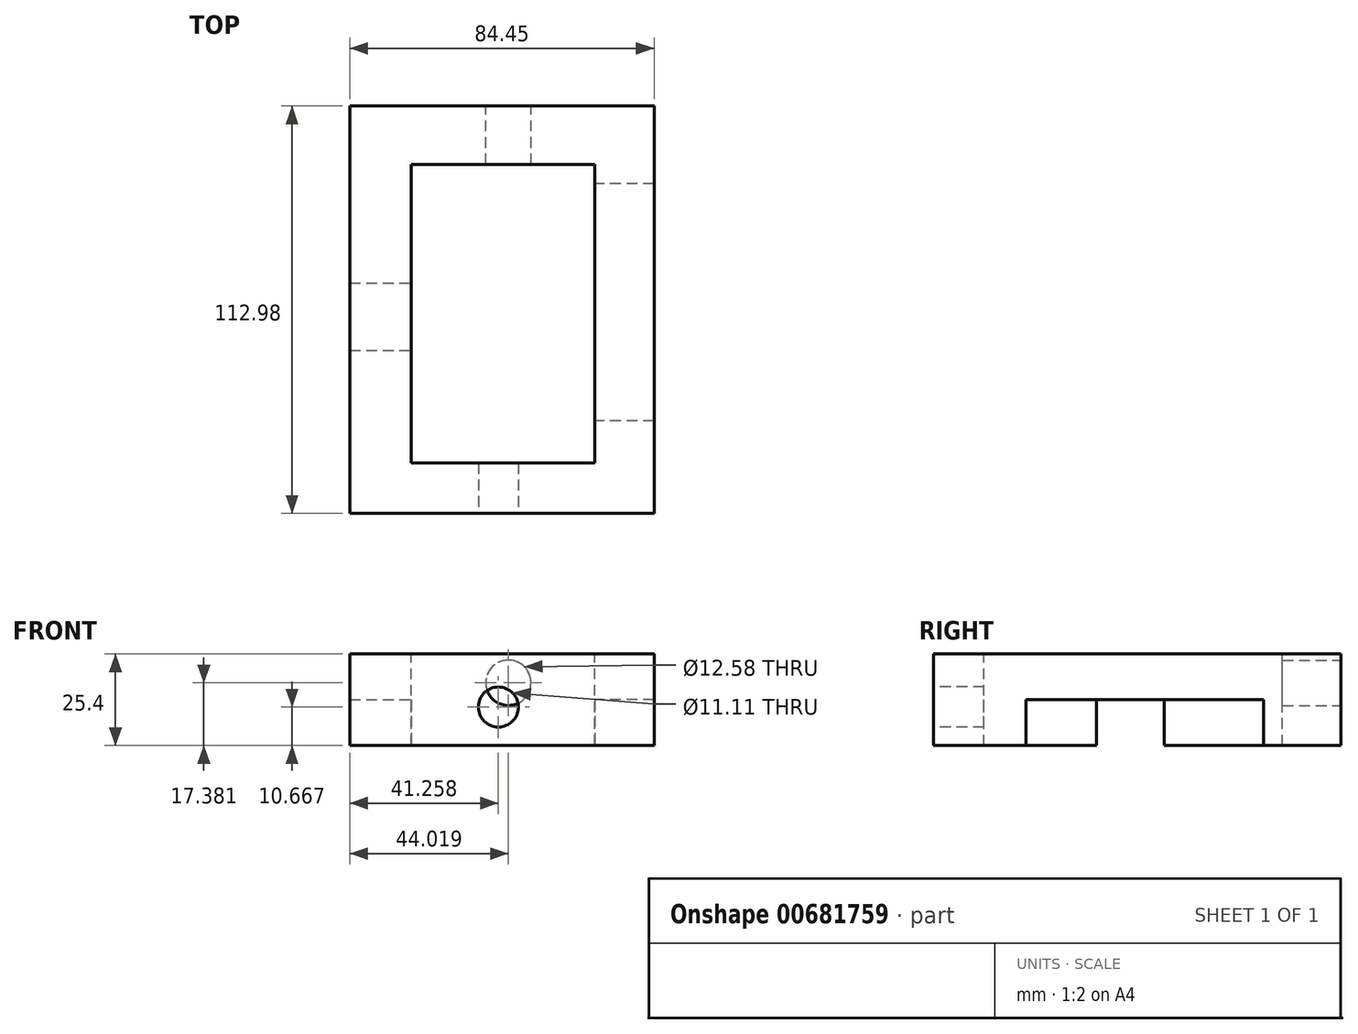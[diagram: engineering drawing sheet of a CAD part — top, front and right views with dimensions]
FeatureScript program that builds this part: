
annotation { "Feature Type Name" : "Feature", "Feature Type Description" : "" }
export const myFeature = defineFeature(function(context is Context, id is Id, definition is map)
    precondition{}
    {
        {
            var Q0;
            Q0=qCreatedBy(makeId("Top.planeOp"),FACE);
            var sketch = newSketch(context, id + "F0", { "sketchPlane" : qUnion([Q0])});
            skLineSegment(sketch, "E0.bottom", {"start": v(-38.24, 59.85) * mm, "end": v(46.21, 59.85) * mm});
            skLineSegment(sketch, "E0.top", {"start": v(-38.24, -53.13) * mm, "end": v(46.21, -53.13) * mm});
            skLineSegment(sketch, "E0.left", {"start": v(-38.24, 59.85) * mm, "end": v(-38.24, -53.13) * mm});
            skLineSegment(sketch, "E0.right", {"start": v(46.21, 59.85) * mm, "end": v(46.21, -53.13) * mm});
            skSolve(sketch);
        }
        {
            var Q0;
            Q0=makeQuery(id+"F0.imprint","IMPRINT",FACE,{"disambiguationData":[TD([[makeQuery(id+"F0.imprint","IMPRINT",EDGE,{"derivedFrom":sQuery(id+"F0.wireOp",EDGE,"E0.bottom")}),-1.0]])]});
            var Q1;
            Q1 = qSketchRegion(id + "F0", true);
            extrude(context, id + "F1", {"entities" : qUnion([Q0, Q1]), "depth" : 25.4 * mm, "offsetDistance" : 25.4 * mm});
        }
        {
            var Q0;
            Q0=makeQuery(id+"F1.opExtrude","CAP_FACE",FACE,{"disambiguationData":[OSD([sQuery(id+"F0.wireOp",EDGE,"E0.bottom"),sQuery(id+"F0.wireOp",EDGE,"E0.top"),sQuery(id+"F0.wireOp",EDGE,"E0.left"),sQuery(id+"F0.wireOp",EDGE,"E0.right")])],"isStart":false});
            var sketch = newSketch(context, id + "F2", { "sketchPlane" : qUnion([Q0])});
            skLineSegment(sketch, "E1.bottom", {"start": v(-21.11, 43.67) * mm, "end": v(29.77, 43.67) * mm});
            skLineSegment(sketch, "E1.top", {"start": v(-21.11, -39.16) * mm, "end": v(29.77, -39.16) * mm});
            skLineSegment(sketch, "E1.left", {"start": v(-21.11, 43.67) * mm, "end": v(-21.11, -39.16) * mm});
            skLineSegment(sketch, "E1.right", {"start": v(29.77, 43.67) * mm, "end": v(29.77, -39.16) * mm});
            skSolve(sketch);
        }
        {
            var Q0;
            Q0=makeQuery(id+"F2.imprint","IMPRINT",FACE,{"disambiguationData":[TD([[makeQuery(id+"F2.imprint","IMPRINT",EDGE,{"derivedFrom":sQuery(id+"F2.wireOp",EDGE,"E1.bottom")}),-1.0]])]});
            extrude(context, id + "F3", {"entities" : qUnion([Q0]), "operationType" : NewBodyOperationType.REMOVE, "oppositeDirection" : true, "depth" : 25.4 * mm, "offsetDistance" : 25.4 * mm});
        }
        {
            var Q0;
            Q0=makeQuery(id+"F1.opExtrude","SWEPT_FACE",FACE,{"disambiguationData":[OSD([sQuery(id+"F0.wireOp",EDGE,"E0.bottom")])]});
            var sketch = newSketch(context, id + "F4", { "sketchPlane" : qUnion([Q0])});
            skCircle(sketch, "E2", {"center": v(-5.78, 17.38) * mm, "radius": 6.29 * mm});
            skSolve(sketch);
        }
        {
            var Q0;
            Q0 = qSketchRegion(id + "F4", true);
            var Q1;
            Q1=makeQuery(id+"F4.imprint","IMPRINT",FACE,{"disambiguationData":[TD([[makeQuery(id+"F4.imprint","IMPRINT",EDGE,{"derivedFrom":sQuery(id+"F4.wireOp",EDGE,"E2")}),1.0]])]});
            extrude(context, id + "F5", {"entities" : qUnion([Q0, Q1]), "operationType" : NewBodyOperationType.REMOVE, "oppositeDirection" : true, "depth" : 25.4 * mm, "offsetDistance" : 25.4 * mm});
        }
        {
            var Q0;
            Q0=makeQuery(id+"F1.opExtrude","SWEPT_FACE",FACE,{"disambiguationData":[OSD([sQuery(id+"F0.wireOp",EDGE,"E0.top")])]});
            var sketch = newSketch(context, id + "F6", { "sketchPlane" : qUnion([Q0])});
            skCircle(sketch, "E3", {"center": v(3.02, 10.67) * mm, "radius": 5.56 * mm});
            skSolve(sketch);
        }
        {
            var Q0;
            Q0 = qSketchRegion(id + "F6", true);
            var Q1;
            Q1=makeQuery(id+"F6.imprint","IMPRINT",FACE,{"disambiguationData":[TD([[makeQuery(id+"F6.imprint","IMPRINT",EDGE,{"derivedFrom":sQuery(id+"F6.wireOp",EDGE,"E3")}),1.0]])]});
            extrude(context, id + "F7", {"entities" : qUnion([Q0, Q1]), "operationType" : NewBodyOperationType.REMOVE, "oppositeDirection" : true, "depth" : 25.4 * mm, "offsetDistance" : 25.4 * mm});
        }
        {
            var Q0;
            Q0=makeQuery(id+"F1.opExtrude","CAP_FACE",FACE,{"disambiguationData":[OSD([sQuery(id+"F0.wireOp",EDGE,"E0.bottom"),sQuery(id+"F0.wireOp",EDGE,"E0.top"),sQuery(id+"F0.wireOp",EDGE,"E0.left"),sQuery(id+"F0.wireOp",EDGE,"E0.right")])],"isStart":true});
            var sketch = newSketch(context, id + "F8", { "sketchPlane" : qUnion([Q0])});
            skLineSegment(sketch, "E4.bottom", {"start": v(-38.24, 7.92) * mm, "end": v(-21.11, 7.92) * mm});
            skLineSegment(sketch, "E4.top", {"start": v(-38.24, -10.82) * mm, "end": v(-21.11, -10.82) * mm});
            skLineSegment(sketch, "E4.left", {"start": v(-38.24, 7.92) * mm, "end": v(-38.24, -10.82) * mm});
            skLineSegment(sketch, "E4.right", {"start": v(-21.11, 7.92) * mm, "end": v(-21.11, -10.82) * mm});
            skSolve(sketch);
        }
        {
            var Q0;
            Q0=makeQuery(id+"F8.imprint","IMPRINT",FACE,{"disambiguationData":[TD([[makeQuery(id+"F8.imprint","IMPRINT",EDGE,{"derivedFrom":sQuery(id+"F8.wireOp",EDGE,"E4.bottom")}),-1.0]])]});
            extrude(context, id + "F9", {"entities" : qUnion([Q0]), "operationType" : NewBodyOperationType.REMOVE, "oppositeDirection" : true, "depth" : 12.7 * mm, "offsetDistance" : 25.4 * mm});
        }
        {
            var Q0;
            Q0=makeQuery(id+"F1.opExtrude","CAP_FACE",FACE,{"disambiguationData":[OSD([sQuery(id+"F0.wireOp",EDGE,"E0.bottom"),sQuery(id+"F0.wireOp",EDGE,"E0.top"),sQuery(id+"F0.wireOp",EDGE,"E0.left"),sQuery(id+"F0.wireOp",EDGE,"E0.right")])],"isStart":true});
            var sketch = newSketch(context, id + "F10", { "sketchPlane" : qUnion([Q0])});
            skLineSegment(sketch, "E5.bottom", {"start": v(46.21, 27.45) * mm, "end": v(29.77, 27.45) * mm});
            skLineSegment(sketch, "E5.top", {"start": v(46.21, -38.35) * mm, "end": v(29.77, -38.35) * mm});
            skLineSegment(sketch, "E5.left", {"start": v(46.21, 27.45) * mm, "end": v(46.21, -38.35) * mm});
            skLineSegment(sketch, "E5.right", {"start": v(29.77, 27.45) * mm, "end": v(29.77, -38.35) * mm});
            skSolve(sketch);
        }
        {
            var Q0;
            Q0=makeQuery(id+"F10.imprint","IMPRINT",FACE,{"disambiguationData":[TD([[makeQuery(id+"F10.imprint","IMPRINT",EDGE,{"derivedFrom":sQuery(id+"F10.wireOp",EDGE,"E5.bottom")}),1.0]])]});
            var Q1;
            Q1 = qSketchRegion(id + "F10", true);
            extrude(context, id + "F11", {"entities" : qUnion([Q0, Q1]), "operationType" : NewBodyOperationType.REMOVE, "oppositeDirection" : true, "depth" : 12.7 * mm, "offsetDistance" : 25.4 * mm});
        }
    });
